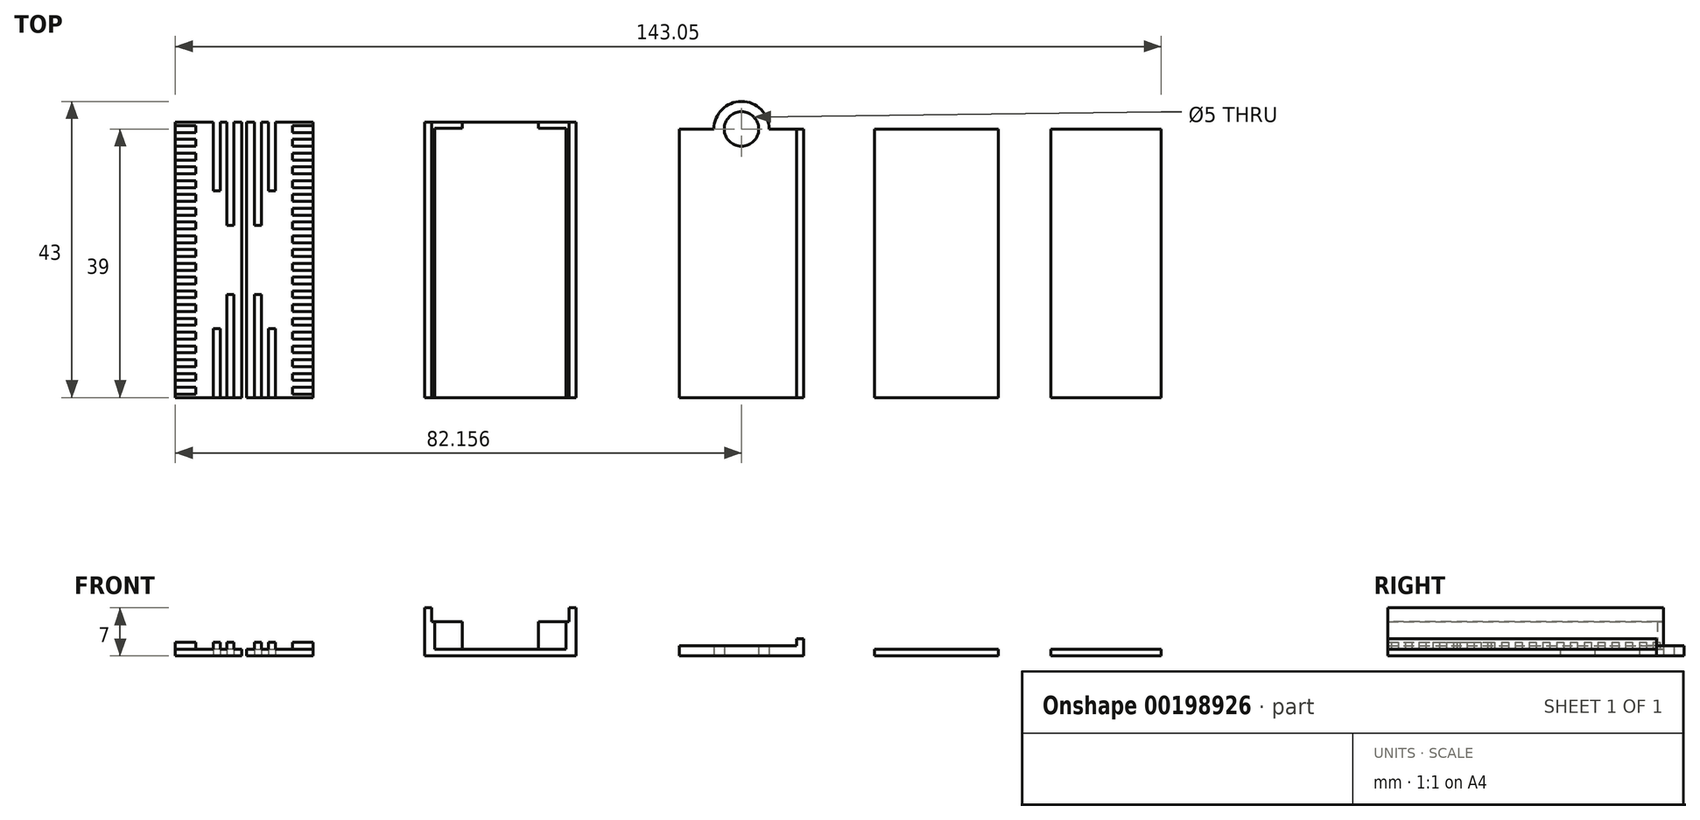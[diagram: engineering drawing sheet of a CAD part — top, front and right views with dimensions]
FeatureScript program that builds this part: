
annotation { "Feature Type Name" : "Feature", "Feature Type Description" : "" }
export const myFeature = defineFeature(function(context is Context, id is Id, definition is map)
    precondition{}
    {
        {
            var Q0;
            Q0=qCreatedBy(makeId("Top.planeOp"),FACE);
            var sketch = newSketch(context, id + "F0", { "sketchPlane" : qUnion([Q0])});
            skLineSegment(sketch, "E0.bottom", {"start": v(-54.83, 0) * mm, "end": v(-34.83, 0) * mm});
            skLineSegment(sketch, "E0.top", {"start": v(-54.83, 40) * mm, "end": v(-34.83, 40) * mm});
            skLineSegment(sketch, "E0.left", {"start": v(-54.83, 0) * mm, "end": v(-54.83, 40) * mm});
            skLineSegment(sketch, "E0.right", {"start": v(-34.83, 0) * mm, "end": v(-34.83, 40) * mm});
            skLineSegment(sketch, "E1.bottom", {"start": v(-18.67, 0) * mm, "end": v(3.33, 0) * mm});
            skLineSegment(sketch, "E1.top", {"start": v(-18.67, 40) * mm, "end": v(3.33, 40) * mm});
            skLineSegment(sketch, "E1.left", {"start": v(-18.67, 0) * mm, "end": v(-18.67, 40) * mm});
            skLineSegment(sketch, "E1.right", {"start": v(3.33, 0) * mm, "end": v(3.33, 40) * mm});
            skLineSegment(sketch, "E2.bottom", {"start": v(46.62, 0) * mm, "end": v(64.62, 0) * mm});
            skLineSegment(sketch, "E2.top", {"start": v(46.62, 39) * mm, "end": v(64.62, 39) * mm});
            skLineSegment(sketch, "E2.left", {"start": v(46.62, 0) * mm, "end": v(46.62, 39) * mm});
            skLineSegment(sketch, "E2.right", {"start": v(64.62, 0) * mm, "end": v(64.62, 39) * mm});
            skLineSegment(sketch, "E3.bottom", {"start": v(18.33, 0) * mm, "end": v(36.33, 0) * mm});
            skLineSegment(sketch, "E3.top", {"start": v(18.33, 39) * mm, "end": v(36.33, 39) * mm});
            skLineSegment(sketch, "E3.left", {"start": v(18.33, 0) * mm, "end": v(18.33, 39) * mm});
            skLineSegment(sketch, "E3.right", {"start": v(36.33, 0) * mm, "end": v(36.33, 39) * mm});
            skLineSegment(sketch, "E4.bottom", {"start": v(72.22, 0) * mm, "end": v(88.22, 0) * mm});
            skLineSegment(sketch, "E4.top", {"start": v(72.22, 39) * mm, "end": v(88.22, 39) * mm});
            skLineSegment(sketch, "E4.left", {"start": v(72.22, 0) * mm, "end": v(72.22, 39) * mm});
            skLineSegment(sketch, "E4.right", {"start": v(88.22, 0) * mm, "end": v(88.22, 39) * mm});
            skLineSegment(sketch, "E5", {"start": v(-17.67, 40) * mm, "end": v(-17.67, 0) * mm});
            skLineSegment(sketch, "E6", {"start": v(2.33, 40) * mm, "end": v(2.33, 0) * mm});
            skLineSegment(sketch, "E7", {"start": v(-17.17, 39.1) * mm, "end": v(-17.17, 0) * mm});
            skLineSegment(sketch, "E8", {"start": v(1.83, 39.1) * mm, "end": v(1.83, 0) * mm});
            skLineSegment(sketch, "E9", {"start": v(-44.83, 40) * mm, "end": v(-44.83, 0) * mm, "construction": true});
            skLineSegment(sketch, "E10.bottom", {"start": v(-44.48, 40) * mm, "end": v(-45.18, 40) * mm});
            skLineSegment(sketch, "E10.top", {"start": v(-44.48, 0) * mm, "end": v(-45.18, 0) * mm});
            skLineSegment(sketch, "E10.left", {"start": v(-44.48, 40) * mm, "end": v(-44.48, 0) * mm});
            skLineSegment(sketch, "E10.right", {"start": v(-45.18, 40) * mm, "end": v(-45.18, 0) * mm});
            skPoint(sketch, "E10.middle", {"position": v(-44.83, 20) * mm});
            skLineSegment(sketch, "E11", {"start": v(-46.83, 40) * mm, "end": v(-46.83, 0) * mm, "construction": true});
            skLineSegment(sketch, "E12", {"start": v(-48.83, 40) * mm, "end": v(-48.83, 0) * mm, "construction": true});
            skLineSegment(sketch, "E13.bottom", {"start": v(-46.33, 40) * mm, "end": v(-47.33, 40) * mm});
            skLineSegment(sketch, "E13.top", {"start": v(-46.33, 25) * mm, "end": v(-47.33, 25) * mm});
            skLineSegment(sketch, "E13.left", {"start": v(-46.33, 40) * mm, "end": v(-46.33, 25) * mm});
            skLineSegment(sketch, "E13.right", {"start": v(-47.33, 40) * mm, "end": v(-47.33, 25) * mm});
            skPoint(sketch, "E13.middle", {"position": v(-46.83, 32.5) * mm});
            skLineSegment(sketch, "E14.bottom", {"start": v(-48.33, 40) * mm, "end": v(-49.33, 40) * mm});
            skLineSegment(sketch, "E14.top", {"start": v(-48.33, 30) * mm, "end": v(-49.33, 30) * mm});
            skLineSegment(sketch, "E14.left", {"start": v(-48.33, 40) * mm, "end": v(-48.33, 30) * mm});
            skLineSegment(sketch, "E14.right", {"start": v(-49.33, 40) * mm, "end": v(-49.33, 30) * mm});
            skPoint(sketch, "E14.middle", {"position": v(-48.83, 35) * mm});
            skLineSegment(sketch, "E15", {"start": v(-34.83, 20) * mm, "end": v(-54.83, 20) * mm, "construction": true});
            skLineSegment(sketch, "E16.MirrorCS", {"start": v(-43.33, 40) * mm, "end": v(-42.33, 40) * mm});
            skLineSegment(sketch, "E17.MirrorCS", {"start": v(-41.33, 40) * mm, "end": v(-40.33, 40) * mm});
            skLineSegment(sketch, "E18.MirrorCS", {"start": v(-41.33, 30) * mm, "end": v(-40.33, 30) * mm});
            skLineSegment(sketch, "E19.MirrorCS", {"start": v(-43.33, 25) * mm, "end": v(-42.33, 25) * mm});
            skLineSegment(sketch, "E20.MirrorCS", {"start": v(-42.33, 40) * mm, "end": v(-42.33, 25) * mm});
            skLineSegment(sketch, "E21.MirrorCS", {"start": v(-40.33, 40) * mm, "end": v(-40.33, 30) * mm});
            skPoint(sketch, "E22.MirrorP", {"position": v(-40.83, 35) * mm});
            skLineSegment(sketch, "E23.MirrorCS", {"start": v(-43.33, 40) * mm, "end": v(-43.33, 25) * mm});
            skLineSegment(sketch, "E24.MirrorCS", {"start": v(-41.33, 40) * mm, "end": v(-41.33, 30) * mm});
            skPoint(sketch, "E25.MirrorP", {"position": v(-42.83, 32.5) * mm});
            skLineSegment(sketch, "E26.MirrorCS", {"start": v(-46.33, 0) * mm, "end": v(-47.33, 0) * mm});
            skLineSegment(sketch, "E27.MirrorCS", {"start": v(-41.33, 0) * mm, "end": v(-40.33, 0) * mm});
            skLineSegment(sketch, "E28.MirrorCS", {"start": v(-41.33, 10) * mm, "end": v(-40.33, 10) * mm});
            skLineSegment(sketch, "E29.MirrorCS", {"start": v(-48.33, 0) * mm, "end": v(-49.33, 0) * mm});
            skLineSegment(sketch, "E30.MirrorCS", {"start": v(-43.33, 0) * mm, "end": v(-42.33, 0) * mm});
            skLineSegment(sketch, "E31.MirrorCS", {"start": v(-48.33, 10) * mm, "end": v(-49.33, 10) * mm});
            skLineSegment(sketch, "E32.MirrorCS", {"start": v(-46.33, 15) * mm, "end": v(-47.33, 15) * mm});
            skLineSegment(sketch, "E33.MirrorCS", {"start": v(-43.33, 15) * mm, "end": v(-42.33, 15) * mm});
            skLineSegment(sketch, "E34.MirrorCS", {"start": v(-47.33, 0) * mm, "end": v(-47.33, 15) * mm});
            skLineSegment(sketch, "E35.MirrorCS", {"start": v(-49.33, 0) * mm, "end": v(-49.33, 10) * mm});
            skLineSegment(sketch, "E36.MirrorCS", {"start": v(-41.33, 0) * mm, "end": v(-41.33, 10) * mm});
            skPoint(sketch, "E37.MirrorP", {"position": v(-48.83, 5) * mm});
            skLineSegment(sketch, "E38.MirrorCS", {"start": v(-46.33, 0) * mm, "end": v(-46.33, 15) * mm});
            skLineSegment(sketch, "E39.MirrorCS", {"start": v(-48.33, 0) * mm, "end": v(-48.33, 10) * mm});
            skLineSegment(sketch, "E40.MirrorCS", {"start": v(-48.83, 0) * mm, "end": v(-48.83, 40) * mm, "construction": true});
            skLineSegment(sketch, "E41.MirrorCS", {"start": v(-43.33, 0) * mm, "end": v(-43.33, 15) * mm});
            skPoint(sketch, "E42.MirrorP", {"position": v(-40.83, 5) * mm});
            skPoint(sketch, "E43.MirrorP", {"position": v(-42.83, 7.5) * mm});
            skLineSegment(sketch, "E44.MirrorCS", {"start": v(-44.83, 0) * mm, "end": v(-44.83, 40) * mm, "construction": true});
            skLineSegment(sketch, "E45.MirrorCS", {"start": v(-45.18, 0) * mm, "end": v(-45.18, 40) * mm});
            skLineSegment(sketch, "E46.MirrorCS", {"start": v(-46.83, 0) * mm, "end": v(-46.83, 40) * mm, "construction": true});
            skLineSegment(sketch, "E47.MirrorCS", {"start": v(-42.33, 0) * mm, "end": v(-42.33, 15) * mm});
            skPoint(sketch, "E48.MirrorP", {"position": v(-46.83, 7.5) * mm});
            skLineSegment(sketch, "E49.MirrorCS", {"start": v(-44.48, 0) * mm, "end": v(-44.48, 40) * mm});
            skLineSegment(sketch, "E50.MirrorCS", {"start": v(-40.33, 0) * mm, "end": v(-40.33, 10) * mm});
            skLineSegment(sketch, "E51.bottom", {"start": v(-54.83, 39.5) * mm, "end": v(-51.83, 39.5) * mm});
            skLineSegment(sketch, "E51.top", {"start": v(-54.83, 38.5) * mm, "end": v(-51.83, 38.5) * mm});
            skLineSegment(sketch, "E51.left", {"start": v(-54.83, 39.5) * mm, "end": v(-54.83, 38.5) * mm});
            skLineSegment(sketch, "E51.right", {"start": v(-51.83, 39.5) * mm, "end": v(-51.83, 38.5) * mm});
            skLineSegment(sketch, "E52.0.1.0", {"start": v(-54.83, 37.5) * mm, "end": v(-51.83, 37.5) * mm});
            skLineSegment(sketch, "E52.0.1.1", {"start": v(-51.83, 37.5) * mm, "end": v(-51.83, 36.5) * mm});
            skLineSegment(sketch, "E52.0.1.2", {"start": v(-54.83, 36.5) * mm, "end": v(-51.83, 36.5) * mm});
            skLineSegment(sketch, "E52.0.2.0", {"start": v(-54.83, 35.5) * mm, "end": v(-51.83, 35.5) * mm});
            skLineSegment(sketch, "E52.0.2.1", {"start": v(-51.83, 35.5) * mm, "end": v(-51.83, 34.5) * mm});
            skLineSegment(sketch, "E52.0.2.2", {"start": v(-54.83, 34.5) * mm, "end": v(-51.83, 34.5) * mm});
            skLineSegment(sketch, "E52.0.3.0", {"start": v(-54.83, 33.5) * mm, "end": v(-51.83, 33.5) * mm});
            skLineSegment(sketch, "E52.0.3.1", {"start": v(-51.83, 33.5) * mm, "end": v(-51.83, 32.5) * mm});
            skLineSegment(sketch, "E52.0.3.2", {"start": v(-54.83, 32.5) * mm, "end": v(-51.83, 32.5) * mm});
            skLineSegment(sketch, "E52.0.4.0", {"start": v(-54.83, 31.5) * mm, "end": v(-51.83, 31.5) * mm});
            skLineSegment(sketch, "E52.0.4.1", {"start": v(-51.83, 31.5) * mm, "end": v(-51.83, 30.5) * mm});
            skLineSegment(sketch, "E52.0.4.2", {"start": v(-54.83, 30.5) * mm, "end": v(-51.83, 30.5) * mm});
            skLineSegment(sketch, "E52.0.5.0", {"start": v(-54.83, 29.5) * mm, "end": v(-51.83, 29.5) * mm});
            skLineSegment(sketch, "E52.0.5.1", {"start": v(-51.83, 29.5) * mm, "end": v(-51.83, 28.5) * mm});
            skLineSegment(sketch, "E52.0.5.2", {"start": v(-54.83, 28.5) * mm, "end": v(-51.83, 28.5) * mm});
            skLineSegment(sketch, "E52.0.6.0", {"start": v(-54.83, 27.5) * mm, "end": v(-51.83, 27.5) * mm});
            skLineSegment(sketch, "E52.0.6.1", {"start": v(-51.83, 27.5) * mm, "end": v(-51.83, 26.5) * mm});
            skLineSegment(sketch, "E52.0.6.2", {"start": v(-54.83, 26.5) * mm, "end": v(-51.83, 26.5) * mm});
            skLineSegment(sketch, "E52.0.7.0", {"start": v(-54.83, 25.5) * mm, "end": v(-51.83, 25.5) * mm});
            skLineSegment(sketch, "E52.0.7.1", {"start": v(-51.83, 25.5) * mm, "end": v(-51.83, 24.5) * mm});
            skLineSegment(sketch, "E52.0.7.2", {"start": v(-54.83, 24.5) * mm, "end": v(-51.83, 24.5) * mm});
            skLineSegment(sketch, "E52.0.8.0", {"start": v(-54.83, 23.5) * mm, "end": v(-51.83, 23.5) * mm});
            skLineSegment(sketch, "E52.0.8.1", {"start": v(-51.83, 23.5) * mm, "end": v(-51.83, 22.5) * mm});
            skLineSegment(sketch, "E52.0.8.2", {"start": v(-54.83, 22.5) * mm, "end": v(-51.83, 22.5) * mm});
            skLineSegment(sketch, "E52.0.9.0", {"start": v(-54.83, 21.5) * mm, "end": v(-51.83, 21.5) * mm});
            skLineSegment(sketch, "E52.0.9.1", {"start": v(-51.83, 21.5) * mm, "end": v(-51.83, 20.5) * mm});
            skLineSegment(sketch, "E52.0.9.2", {"start": v(-54.83, 20.5) * mm, "end": v(-51.83, 20.5) * mm});
            skLineSegment(sketch, "E52.0.10.0", {"start": v(-54.83, 19.5) * mm, "end": v(-51.83, 19.5) * mm});
            skLineSegment(sketch, "E52.0.10.1", {"start": v(-51.83, 19.5) * mm, "end": v(-51.83, 18.5) * mm});
            skLineSegment(sketch, "E52.0.10.2", {"start": v(-54.83, 18.5) * mm, "end": v(-51.83, 18.5) * mm});
            skLineSegment(sketch, "E52.0.11.0", {"start": v(-54.83, 17.5) * mm, "end": v(-51.83, 17.5) * mm});
            skLineSegment(sketch, "E52.0.11.1", {"start": v(-51.83, 17.5) * mm, "end": v(-51.83, 16.5) * mm});
            skLineSegment(sketch, "E52.0.11.2", {"start": v(-54.83, 16.5) * mm, "end": v(-51.83, 16.5) * mm});
            skLineSegment(sketch, "E52.0.12.0", {"start": v(-54.83, 15.5) * mm, "end": v(-51.83, 15.5) * mm});
            skLineSegment(sketch, "E52.0.12.1", {"start": v(-51.83, 15.5) * mm, "end": v(-51.83, 14.5) * mm});
            skLineSegment(sketch, "E52.0.12.2", {"start": v(-54.83, 14.5) * mm, "end": v(-51.83, 14.5) * mm});
            skLineSegment(sketch, "E52.0.13.0", {"start": v(-54.83, 13.5) * mm, "end": v(-51.83, 13.5) * mm});
            skLineSegment(sketch, "E52.0.13.1", {"start": v(-51.83, 13.5) * mm, "end": v(-51.83, 12.5) * mm});
            skLineSegment(sketch, "E52.0.13.2", {"start": v(-54.83, 12.5) * mm, "end": v(-51.83, 12.5) * mm});
            skLineSegment(sketch, "E52.0.14.0", {"start": v(-54.83, 11.5) * mm, "end": v(-51.83, 11.5) * mm});
            skLineSegment(sketch, "E52.0.14.1", {"start": v(-51.83, 11.5) * mm, "end": v(-51.83, 10.5) * mm});
            skLineSegment(sketch, "E52.0.14.2", {"start": v(-54.83, 10.5) * mm, "end": v(-51.83, 10.5) * mm});
            skLineSegment(sketch, "E52.0.15.0", {"start": v(-54.83, 9.5) * mm, "end": v(-51.83, 9.5) * mm});
            skLineSegment(sketch, "E52.0.15.1", {"start": v(-51.83, 9.5) * mm, "end": v(-51.83, 8.5) * mm});
            skLineSegment(sketch, "E52.0.15.2", {"start": v(-54.83, 8.5) * mm, "end": v(-51.83, 8.5) * mm});
            skLineSegment(sketch, "E52.0.16.0", {"start": v(-54.83, 7.5) * mm, "end": v(-51.83, 7.5) * mm});
            skLineSegment(sketch, "E52.0.16.1", {"start": v(-51.83, 7.5) * mm, "end": v(-51.83, 6.5) * mm});
            skLineSegment(sketch, "E52.0.16.2", {"start": v(-54.83, 6.5) * mm, "end": v(-51.83, 6.5) * mm});
            skLineSegment(sketch, "E52.0.17.0", {"start": v(-54.83, 5.5) * mm, "end": v(-51.83, 5.5) * mm});
            skLineSegment(sketch, "E52.0.17.1", {"start": v(-51.83, 5.5) * mm, "end": v(-51.83, 4.5) * mm});
            skLineSegment(sketch, "E52.0.17.2", {"start": v(-54.83, 4.5) * mm, "end": v(-51.83, 4.5) * mm});
            skLineSegment(sketch, "E52.0.18.0", {"start": v(-54.83, 3.5) * mm, "end": v(-51.83, 3.5) * mm});
            skLineSegment(sketch, "E52.0.18.1", {"start": v(-51.83, 3.5) * mm, "end": v(-51.83, 2.5) * mm});
            skLineSegment(sketch, "E52.0.18.2", {"start": v(-54.83, 2.5) * mm, "end": v(-51.83, 2.5) * mm});
            skLineSegment(sketch, "E52.0.19.0", {"start": v(-54.83, 1.5) * mm, "end": v(-51.83, 1.5) * mm});
            skLineSegment(sketch, "E52.0.19.1", {"start": v(-51.83, 1.5) * mm, "end": v(-51.83, 0.5) * mm});
            skLineSegment(sketch, "E52.0.19.2", {"start": v(-54.83, 0.5) * mm, "end": v(-51.83, 0.5) * mm});
            skLineSegment(sketch, "E52.direction1", {"start": v(-54.83, 39.5) * mm, "end": v(-51.93, 39.5) * mm, "construction": true});
            skLineSegment(sketch, "E52.direction2", {"start": v(-54.83, 39.5) * mm, "end": v(-54.83, 37.5) * mm, "construction": true});
            skLineSegment(sketch, "E53.MirrorCS", {"start": v(-37.83, 27.5) * mm, "end": v(-37.83, 26.5) * mm});
            skLineSegment(sketch, "E54.MirrorCS", {"start": v(-37.83, 19.5) * mm, "end": v(-37.83, 18.5) * mm});
            skLineSegment(sketch, "E55.MirrorCS", {"start": v(-37.83, 15.5) * mm, "end": v(-37.83, 14.5) * mm});
            skLineSegment(sketch, "E56.MirrorCS", {"start": v(-37.83, 9.5) * mm, "end": v(-37.83, 8.5) * mm});
            skLineSegment(sketch, "E57.MirrorCS", {"start": v(-37.83, 31.5) * mm, "end": v(-37.83, 30.5) * mm});
            skLineSegment(sketch, "E58.MirrorCS", {"start": v(-37.83, 21.5) * mm, "end": v(-37.83, 20.5) * mm});
            skLineSegment(sketch, "E59.MirrorCS", {"start": v(-37.83, 37.5) * mm, "end": v(-37.83, 36.5) * mm});
            skLineSegment(sketch, "E60.MirrorCS", {"start": v(-37.83, 25.5) * mm, "end": v(-37.83, 24.5) * mm});
            skLineSegment(sketch, "E61.MirrorCS", {"start": v(-37.83, 11.5) * mm, "end": v(-37.83, 10.5) * mm});
            skLineSegment(sketch, "E62.MirrorCS", {"start": v(-37.83, 35.5) * mm, "end": v(-37.83, 34.5) * mm});
            skLineSegment(sketch, "E63.MirrorCS", {"start": v(-37.83, 23.5) * mm, "end": v(-37.83, 22.5) * mm});
            skLineSegment(sketch, "E64.MirrorCS", {"start": v(-37.83, 13.5) * mm, "end": v(-37.83, 12.5) * mm});
            skLineSegment(sketch, "E65.MirrorCS", {"start": v(-37.83, 29.5) * mm, "end": v(-37.83, 28.5) * mm});
            skLineSegment(sketch, "E66.MirrorCS", {"start": v(-37.83, 17.5) * mm, "end": v(-37.83, 16.5) * mm});
            skLineSegment(sketch, "E67.MirrorCS", {"start": v(-37.83, 33.5) * mm, "end": v(-37.83, 32.5) * mm});
            skLineSegment(sketch, "E68.MirrorCS", {"start": v(-37.83, 39.5) * mm, "end": v(-37.83, 38.5) * mm});
            skLineSegment(sketch, "E69.MirrorCS", {"start": v(-34.83, 39.5) * mm, "end": v(-37.83, 39.5) * mm});
            skLineSegment(sketch, "E70.MirrorCS", {"start": v(-34.83, 16.5) * mm, "end": v(-37.83, 16.5) * mm});
            skLineSegment(sketch, "E71.MirrorCS", {"start": v(-34.83, 37.5) * mm, "end": v(-37.83, 37.5) * mm});
            skLineSegment(sketch, "E72.MirrorCS", {"start": v(-34.83, 36.5) * mm, "end": v(-37.83, 36.5) * mm});
            skLineSegment(sketch, "E73.MirrorCS", {"start": v(-34.83, 29.5) * mm, "end": v(-37.83, 29.5) * mm});
            skLineSegment(sketch, "E74.MirrorCS", {"start": v(-34.83, 8.5) * mm, "end": v(-37.83, 8.5) * mm});
            skLineSegment(sketch, "E75.MirrorCS", {"start": v(-54.83, 20) * mm, "end": v(-34.83, 20) * mm, "construction": true});
            skLineSegment(sketch, "E76.MirrorCS", {"start": v(-34.83, 25.5) * mm, "end": v(-37.83, 25.5) * mm});
            skLineSegment(sketch, "E77.MirrorCS", {"start": v(-34.83, 19.5) * mm, "end": v(-37.83, 19.5) * mm});
            skLineSegment(sketch, "E78.MirrorCS", {"start": v(-34.83, 30.5) * mm, "end": v(-37.83, 30.5) * mm});
            skLineSegment(sketch, "E79.MirrorCS", {"start": v(-34.83, 20.5) * mm, "end": v(-37.83, 20.5) * mm});
            skLineSegment(sketch, "E80.MirrorCS", {"start": v(-34.83, 9.5) * mm, "end": v(-37.83, 9.5) * mm});
            skLineSegment(sketch, "E81.MirrorCS", {"start": v(-34.83, 10.5) * mm, "end": v(-37.83, 10.5) * mm});
            skLineSegment(sketch, "E82.MirrorCS", {"start": v(-34.83, 39.5) * mm, "end": v(-37.73, 39.5) * mm, "construction": true});
            skLineSegment(sketch, "E83.MirrorCS", {"start": v(-34.83, 15.5) * mm, "end": v(-37.83, 15.5) * mm});
            skLineSegment(sketch, "E84.MirrorCS", {"start": v(-34.83, 26.5) * mm, "end": v(-37.83, 26.5) * mm});
            skLineSegment(sketch, "E85.MirrorCS", {"start": v(-34.83, 31.5) * mm, "end": v(-37.83, 31.5) * mm});
            skLineSegment(sketch, "E86.MirrorCS", {"start": v(-34.83, 35.5) * mm, "end": v(-37.83, 35.5) * mm});
            skLineSegment(sketch, "E87.MirrorCS", {"start": v(-34.83, 14.5) * mm, "end": v(-37.83, 14.5) * mm});
            skLineSegment(sketch, "E88.MirrorCS", {"start": v(-34.83, 21.5) * mm, "end": v(-37.83, 21.5) * mm});
            skLineSegment(sketch, "E89.MirrorCS", {"start": v(-34.83, 32.5) * mm, "end": v(-37.83, 32.5) * mm});
            skLineSegment(sketch, "E90.MirrorCS", {"start": v(-34.83, 13.5) * mm, "end": v(-37.83, 13.5) * mm});
            skLineSegment(sketch, "E91.MirrorCS", {"start": v(-34.83, 24.5) * mm, "end": v(-37.83, 24.5) * mm});
            skLineSegment(sketch, "E92.MirrorCS", {"start": v(-34.83, 33.5) * mm, "end": v(-37.83, 33.5) * mm});
            skLineSegment(sketch, "E93.MirrorCS", {"start": v(-34.83, 12.5) * mm, "end": v(-37.83, 12.5) * mm});
            skLineSegment(sketch, "E94.MirrorCS", {"start": v(-34.83, 23.5) * mm, "end": v(-37.83, 23.5) * mm});
            skLineSegment(sketch, "E95.MirrorCS", {"start": v(-34.83, 18.5) * mm, "end": v(-37.83, 18.5) * mm});
            skLineSegment(sketch, "E96.MirrorCS", {"start": v(-34.83, 38.5) * mm, "end": v(-37.83, 38.5) * mm});
            skLineSegment(sketch, "E97.MirrorCS", {"start": v(-34.83, 27.5) * mm, "end": v(-37.83, 27.5) * mm});
            skLineSegment(sketch, "E98.MirrorCS", {"start": v(-34.83, 34.5) * mm, "end": v(-37.83, 34.5) * mm});
            skLineSegment(sketch, "E99.MirrorCS", {"start": v(-34.83, 11.5) * mm, "end": v(-37.83, 11.5) * mm});
            skLineSegment(sketch, "E100.MirrorCS", {"start": v(-34.83, 17.5) * mm, "end": v(-37.83, 17.5) * mm});
            skLineSegment(sketch, "E101.MirrorCS", {"start": v(-34.83, 28.5) * mm, "end": v(-37.83, 28.5) * mm});
            skLineSegment(sketch, "E102.MirrorCS", {"start": v(-34.83, 22.5) * mm, "end": v(-37.83, 22.5) * mm});
            skLineSegment(sketch, "E103.MirrorCS", {"start": v(-37.83, 1.5) * mm, "end": v(-37.83, 0.5) * mm});
            skLineSegment(sketch, "E104.MirrorCS", {"start": v(-34.83, 1.5) * mm, "end": v(-37.83, 1.5) * mm});
            skLineSegment(sketch, "E105.MirrorCS", {"start": v(-37.83, 7.5) * mm, "end": v(-37.83, 6.5) * mm});
            skLineSegment(sketch, "E106.MirrorCS", {"start": v(-34.83, 5.5) * mm, "end": v(-37.83, 5.5) * mm});
            skLineSegment(sketch, "E107.MirrorCS", {"start": v(-34.83, 4.5) * mm, "end": v(-37.83, 4.5) * mm});
            skLineSegment(sketch, "E108.MirrorCS", {"start": v(-34.83, 7.5) * mm, "end": v(-37.83, 7.5) * mm});
            skLineSegment(sketch, "E109.MirrorCS", {"start": v(-37.83, 5.5) * mm, "end": v(-37.83, 4.5) * mm});
            skLineSegment(sketch, "E110.MirrorCS", {"start": v(-34.83, 3.5) * mm, "end": v(-37.83, 3.5) * mm});
            skLineSegment(sketch, "E111.MirrorCS", {"start": v(-37.83, 3.5) * mm, "end": v(-37.83, 2.5) * mm});
            skLineSegment(sketch, "E112.MirrorCS", {"start": v(-34.83, 2.5) * mm, "end": v(-37.83, 2.5) * mm});
            skLineSegment(sketch, "E113.MirrorCS", {"start": v(-34.83, 0.5) * mm, "end": v(-37.83, 0.5) * mm});
            skLineSegment(sketch, "E114.MirrorCS", {"start": v(-34.83, 6.5) * mm, "end": v(-37.83, 6.5) * mm});
            skCircle(sketch, "E115", {"center": v(27.33, 39) * mm, "radius": 2.5 * mm});
            skCircle(sketch, "E116", {"center": v(27.33, 39) * mm, "radius": 4 * mm});
            skLineSegment(sketch, "E117", {"start": v(35.33, 39) * mm, "end": v(35.33, 0) * mm});
            skLineSegment(sketch, "E118.bottom", {"start": v(1.83, 40) * mm, "end": v(-2.17, 40) * mm});
            skLineSegment(sketch, "E118.top", {"start": v(1.83, 39.1) * mm, "end": v(-2.17, 39.1) * mm});
            skLineSegment(sketch, "E118.right", {"start": v(-2.17, 40) * mm, "end": v(-2.17, 39.1) * mm});
            skLineSegment(sketch, "E119.bottom", {"start": v(-17.17, 40) * mm, "end": v(-13.17, 40) * mm});
            skLineSegment(sketch, "E119.top", {"start": v(-17.17, 39.1) * mm, "end": v(-13.17, 39.1) * mm});
            skLineSegment(sketch, "E119.right", {"start": v(-13.17, 40) * mm, "end": v(-13.17, 39.1) * mm});
            skSolve(sketch);
        }
        {
            var Q0;
            {var subQ0=sQuery(id+"F0.wireOp",EDGE,"E52.0.10.0");Q0=makeQuery(id+"F0.imprint","IMPRINT",FACE,{"disambiguationData":[TD([[makeQuery(id+"F0.imprint","IMPRINT",EDGE,{"derivedFrom":subQ0}),-1.0]])]});}
            var Q1;
            {var subQ0=sQuery(id+"F0.wireOp",EDGE,"E52.0.11.0");Q1=makeQuery(id+"F0.imprint","IMPRINT",FACE,{"disambiguationData":[TD([[makeQuery(id+"F0.imprint","IMPRINT",EDGE,{"derivedFrom":subQ0}),-1.0]])]});}
            var Q2;
            Q2=makeQuery(id+"F0.imprint","IMPRINT",FACE,{"disambiguationData":[TD([[makeQuery(id+"F0.imprint","IMPRINT",EDGE,{"derivedFrom":sQuery(id+"F0.wireOp",EDGE,"E61.MirrorCS")}),1.0]])]});
            var Q3;
            {var subQ0=sQuery(id+"F0.wireOp",EDGE,"E52.0.12.0");Q3=makeQuery(id+"F0.imprint","IMPRINT",FACE,{"disambiguationData":[TD([[makeQuery(id+"F0.imprint","IMPRINT",EDGE,{"derivedFrom":subQ0}),-1.0]])]});}
            var Q4;
            {var subQ0=sQuery(id+"F0.wireOp",EDGE,"E52.0.13.0");Q4=makeQuery(id+"F0.imprint","IMPRINT",FACE,{"disambiguationData":[TD([[makeQuery(id+"F0.imprint","IMPRINT",EDGE,{"derivedFrom":subQ0}),-1.0]])]});}
            var Q5;
            Q5=makeQuery(id+"F0.imprint","IMPRINT",FACE,{"disambiguationData":[TD([[makeQuery(id+"F0.imprint","IMPRINT",EDGE,{"derivedFrom":sQuery(id+"F0.wireOp",EDGE,"E65.MirrorCS")}),1.0]])]});
            var Q6;
            {var subQ0=sQuery(id+"F0.wireOp",EDGE,"E106.MirrorCS");Q6=makeQuery(id+"F0.imprint","IMPRINT",FACE,{"disambiguationData":[TD([[makeQuery(id+"F0.imprint","IMPRINT",EDGE,{"derivedFrom":subQ0}),1.0]])]});}
            var Q7;
            Q7=makeQuery(id+"F0.imprint","IMPRINT",FACE,{"disambiguationData":[TD([[makeQuery(id+"F0.imprint","IMPRINT",EDGE,{"derivedFrom":sQuery(id+"F0.wireOp",EDGE,"E66.MirrorCS")}),1.0]])]});
            var Q8;
            Q8=makeQuery(id+"F0.imprint","IMPRINT",FACE,{"disambiguationData":[TD([[makeQuery(id+"F0.imprint","IMPRINT",EDGE,{"derivedFrom":sQuery(id+"F0.wireOp",EDGE,"E16.MirrorCS")}),-1.0]])]});
            var Q9;
            Q9=makeQuery(id+"F0.imprint","IMPRINT",FACE,{"disambiguationData":[TD([[makeQuery(id+"F0.imprint","IMPRINT",EDGE,{"derivedFrom":sQuery(id+"F0.wireOp",EDGE,"E51.bottom")}),-1.0]])]});
            var Q10;
            {var subQ0=sQuery(id+"F0.wireOp",EDGE,"E110.MirrorCS");Q10=makeQuery(id+"F0.imprint","IMPRINT",FACE,{"disambiguationData":[TD([[makeQuery(id+"F0.imprint","IMPRINT",EDGE,{"derivedFrom":subQ0}),1.0]])]});}
            var Q11;
            Q11=makeQuery(id+"F0.imprint","IMPRINT",FACE,{"disambiguationData":[TD([[makeQuery(id+"F0.imprint","IMPRINT",EDGE,{"derivedFrom":sQuery(id+"F0.wireOp",EDGE,"E62.MirrorCS")}),1.0]])]});
            var Q12;
            {var subQ0=sQuery(id+"F0.wireOp",EDGE,"E52.0.14.0");Q12=makeQuery(id+"F0.imprint","IMPRINT",FACE,{"disambiguationData":[TD([[makeQuery(id+"F0.imprint","IMPRINT",EDGE,{"derivedFrom":subQ0}),-1.0]])]});}
            var Q13;
            Q13=makeQuery(id+"F0.imprint","IMPRINT",FACE,{"disambiguationData":[TD([[makeQuery(id+"F0.imprint","IMPRINT",EDGE,{"derivedFrom":sQuery(id+"F0.wireOp",EDGE,"E59.MirrorCS")}),1.0]])]});
            var Q14;
            Q14=makeQuery(id+"F0.imprint","IMPRINT",FACE,{"disambiguationData":[TD([[makeQuery(id+"F0.imprint","IMPRINT",EDGE,{"derivedFrom":sQuery(id+"F0.wireOp",EDGE,"E10.bottom")}),1.0]])]});
            var Q15;
            {var subQ0=sQuery(id+"F0.wireOp",EDGE,"E52.0.15.0");Q15=makeQuery(id+"F0.imprint","IMPRINT",FACE,{"disambiguationData":[TD([[makeQuery(id+"F0.imprint","IMPRINT",EDGE,{"derivedFrom":subQ0}),-1.0]])]});}
            var Q16;
            {var subQ0=sQuery(id+"F0.wireOp",EDGE,"E52.0.16.0");Q16=makeQuery(id+"F0.imprint","IMPRINT",FACE,{"disambiguationData":[TD([[makeQuery(id+"F0.imprint","IMPRINT",EDGE,{"derivedFrom":subQ0}),-1.0]])]});}
            var Q17;
            Q17=makeQuery(id+"F0.imprint","IMPRINT",FACE,{"disambiguationData":[TD([[makeQuery(id+"F0.imprint","IMPRINT",EDGE,{"derivedFrom":sQuery(id+"F0.wireOp",EDGE,"E13.bottom")}),1.0]])]});
            var Q18;
            Q18=makeQuery(id+"F0.imprint","IMPRINT",FACE,{"disambiguationData":[TD([[makeQuery(id+"F0.imprint","IMPRINT",EDGE,{"derivedFrom":sQuery(id+"F0.wireOp",EDGE,"E64.MirrorCS")}),1.0]])]});
            var Q19;
            {var subQ0=sQuery(id+"F0.wireOp",EDGE,"E52.0.17.0");Q19=makeQuery(id+"F0.imprint","IMPRINT",FACE,{"disambiguationData":[TD([[makeQuery(id+"F0.imprint","IMPRINT",EDGE,{"derivedFrom":subQ0}),-1.0]])]});}
            var Q20;
            {var subQ0=sQuery(id+"F0.wireOp",EDGE,"E52.0.18.0");Q20=makeQuery(id+"F0.imprint","IMPRINT",FACE,{"disambiguationData":[TD([[makeQuery(id+"F0.imprint","IMPRINT",EDGE,{"derivedFrom":subQ0}),-1.0]])]});}
            var Q21;
            {var subQ0=sQuery(id+"F0.wireOp",EDGE,"E52.0.6.0");Q21=makeQuery(id+"F0.imprint","IMPRINT",FACE,{"disambiguationData":[TD([[makeQuery(id+"F0.imprint","IMPRINT",EDGE,{"derivedFrom":subQ0}),-1.0]])]});}
            var Q22;
            Q22=makeQuery(id+"F0.imprint","IMPRINT",FACE,{"disambiguationData":[TD([[makeQuery(id+"F0.imprint","IMPRINT",EDGE,{"derivedFrom":sQuery(id+"F0.wireOp",EDGE,"E28.MirrorCS")}),-1.0]])]});
            var Q23;
            Q23=makeQuery(id+"F0.imprint","IMPRINT",FACE,{"disambiguationData":[TD([[makeQuery(id+"F0.imprint","IMPRINT",EDGE,{"derivedFrom":sQuery(id+"F0.wireOp",EDGE,"E58.MirrorCS")}),1.0]])]});
            var Q24;
            {var subQ0=sQuery(id+"F0.wireOp",EDGE,"E52.0.19.0");Q24=makeQuery(id+"F0.imprint","IMPRINT",FACE,{"disambiguationData":[TD([[makeQuery(id+"F0.imprint","IMPRINT",EDGE,{"derivedFrom":subQ0}),-1.0]])]});}
            var Q25;
            {var subQ0=sQuery(id+"F0.wireOp",EDGE,"E52.0.8.0");Q25=makeQuery(id+"F0.imprint","IMPRINT",FACE,{"disambiguationData":[TD([[makeQuery(id+"F0.imprint","IMPRINT",EDGE,{"derivedFrom":subQ0}),-1.0]])]});}
            var Q26;
            {var subQ0=sQuery(id+"F0.wireOp",EDGE,"E52.0.9.0");Q26=makeQuery(id+"F0.imprint","IMPRINT",FACE,{"disambiguationData":[TD([[makeQuery(id+"F0.imprint","IMPRINT",EDGE,{"derivedFrom":subQ0}),-1.0]])]});}
            var Q27;
            {var subQ0=sQuery(id+"F0.wireOp",EDGE,"E52.0.7.0");Q27=makeQuery(id+"F0.imprint","IMPRINT",FACE,{"disambiguationData":[TD([[makeQuery(id+"F0.imprint","IMPRINT",EDGE,{"derivedFrom":subQ0}),-1.0]])]});}
            var Q28;
            Q28=makeQuery(id+"F0.imprint","IMPRINT",FACE,{"disambiguationData":[TD([[makeQuery(id+"F0.imprint","IMPRINT",EDGE,{"derivedFrom":sQuery(id+"F0.wireOp",EDGE,"E103.MirrorCS")}),1.0]])]});
            var Q29;
            Q29=makeQuery(id+"F0.imprint","IMPRINT",FACE,{"disambiguationData":[TD([[makeQuery(id+"F0.imprint","IMPRINT",EDGE,{"derivedFrom":sQuery(id+"F0.wireOp",EDGE,"E67.MirrorCS")}),1.0]])]});
            var Q30;
            {var subQ0=sQuery(id+"F0.wireOp",EDGE,"E52.0.5.0");Q30=makeQuery(id+"F0.imprint","IMPRINT",FACE,{"disambiguationData":[TD([[makeQuery(id+"F0.imprint","IMPRINT",EDGE,{"derivedFrom":subQ0}),-1.0]])]});}
            var Q31;
            Q31=makeQuery(id+"F0.imprint","IMPRINT",FACE,{"disambiguationData":[TD([[makeQuery(id+"F0.imprint","IMPRINT",EDGE,{"derivedFrom":sQuery(id+"F0.wireOp",EDGE,"E31.MirrorCS")}),1.0]])]});
            var Q32;
            Q32=makeQuery(id+"F0.imprint","IMPRINT",FACE,{"disambiguationData":[TD([[makeQuery(id+"F0.imprint","IMPRINT",EDGE,{"derivedFrom":sQuery(id+"F0.wireOp",EDGE,"E63.MirrorCS")}),1.0]])]});
            var Q33;
            {var subQ0=sQuery(id+"F0.wireOp",EDGE,"E52.0.4.0");Q33=makeQuery(id+"F0.imprint","IMPRINT",FACE,{"disambiguationData":[TD([[makeQuery(id+"F0.imprint","IMPRINT",EDGE,{"derivedFrom":subQ0}),-1.0]])]});}
            var Q34;
            Q34=makeQuery(id+"F0.imprint","IMPRINT",FACE,{"disambiguationData":[TD([[makeQuery(id+"F0.imprint","IMPRINT",EDGE,{"derivedFrom":sQuery(id+"F0.wireOp",EDGE,"E60.MirrorCS")}),1.0]])]});
            var Q35;
            Q35=makeQuery(id+"F0.imprint","IMPRINT",FACE,{"disambiguationData":[TD([[makeQuery(id+"F0.imprint","IMPRINT",EDGE,{"derivedFrom":sQuery(id+"F0.wireOp",EDGE,"E32.MirrorCS")}),1.0]])]});
            var Q36;
            {var subQ0=sQuery(id+"F0.wireOp",EDGE,"E52.0.3.0");Q36=makeQuery(id+"F0.imprint","IMPRINT",FACE,{"disambiguationData":[TD([[makeQuery(id+"F0.imprint","IMPRINT",EDGE,{"derivedFrom":subQ0}),-1.0]])]});}
            var Q37;
            Q37=makeQuery(id+"F0.imprint","IMPRINT",FACE,{"disambiguationData":[TD([[makeQuery(id+"F0.imprint","IMPRINT",EDGE,{"derivedFrom":sQuery(id+"F0.wireOp",EDGE,"E33.MirrorCS")}),-1.0]])]});
            var Q38;
            Q38=makeQuery(id+"F0.imprint","IMPRINT",FACE,{"disambiguationData":[TD([[makeQuery(id+"F0.imprint","IMPRINT",EDGE,{"derivedFrom":sQuery(id+"F0.wireOp",EDGE,"E53.MirrorCS")}),1.0]])]});
            var Q39;
            Q39=makeQuery(id+"F0.imprint","IMPRINT",FACE,{"disambiguationData":[TD([[makeQuery(id+"F0.imprint","IMPRINT",EDGE,{"derivedFrom":sQuery(id+"F0.wireOp",EDGE,"E57.MirrorCS")}),1.0]])]});
            var Q40;
            {var subQ0=sQuery(id+"F0.wireOp",EDGE,"E52.0.1.0");Q40=makeQuery(id+"F0.imprint","IMPRINT",FACE,{"disambiguationData":[TD([[makeQuery(id+"F0.imprint","IMPRINT",EDGE,{"derivedFrom":subQ0}),-1.0]])]});}
            var Q41;
            {var subQ0=sQuery(id+"F0.wireOp",EDGE,"E52.0.2.0");Q41=makeQuery(id+"F0.imprint","IMPRINT",FACE,{"disambiguationData":[TD([[makeQuery(id+"F0.imprint","IMPRINT",EDGE,{"derivedFrom":subQ0}),-1.0]])]});}
            var Q42;
            Q42=makeQuery(id+"F0.imprint","IMPRINT",FACE,{"disambiguationData":[TD([[makeQuery(id+"F0.imprint","IMPRINT",EDGE,{"derivedFrom":sQuery(id+"F0.wireOp",EDGE,"E55.MirrorCS")}),1.0]])]});
            var Q43;
            Q43=makeQuery(id+"F0.imprint","IMPRINT",FACE,{"disambiguationData":[TD([[makeQuery(id+"F0.imprint","IMPRINT",EDGE,{"derivedFrom":sQuery(id+"F0.wireOp",EDGE,"E14.bottom")}),1.0]])]});
            var Q44;
            Q44=makeQuery(id+"F0.imprint","IMPRINT",FACE,{"disambiguationData":[TD([[makeQuery(id+"F0.imprint","IMPRINT",EDGE,{"derivedFrom":sQuery(id+"F0.wireOp",EDGE,"E56.MirrorCS")}),1.0]])]});
            var Q45;
            Q45=makeQuery(id+"F0.imprint","IMPRINT",FACE,{"disambiguationData":[TD([[makeQuery(id+"F0.imprint","IMPRINT",EDGE,{"derivedFrom":sQuery(id+"F0.wireOp",EDGE,"E18.MirrorCS")}),-1.0]])]});
            var Q46;
            Q46=makeQuery(id+"F0.imprint","IMPRINT",FACE,{"disambiguationData":[TD([[makeQuery(id+"F0.imprint","IMPRINT",EDGE,{"derivedFrom":sQuery(id+"F0.wireOp",EDGE,"E54.MirrorCS")}),1.0]])]});
            var Q47;
            Q47=makeQuery(id+"F0.imprint","IMPRINT",FACE,{"disambiguationData":[TD([[makeQuery(id+"F0.imprint","IMPRINT",EDGE,{"derivedFrom":sQuery(id+"F0.wireOp",EDGE,"E13.top")}),1.0]])]});
            var Q48;
            Q48=makeQuery(id+"F0.imprint","IMPRINT",FACE,{"disambiguationData":[TD([[makeQuery(id+"F0.imprint","IMPRINT",EDGE,{"derivedFrom":sQuery(id+"F0.wireOp",EDGE,"E68.MirrorCS")}),1.0]])]});
            var Q49;
            Q49=makeQuery(id+"F0.imprint","IMPRINT",FACE,{"disambiguationData":[TD([[makeQuery(id+"F0.imprint","IMPRINT",EDGE,{"derivedFrom":sQuery(id+"F0.wireOp",EDGE,"E105.MirrorCS")}),1.0]])]});
            var Q50;
            Q50=makeQuery(id+"F0.imprint","IMPRINT",FACE,{"disambiguationData":[TD([[makeQuery(id+"F0.imprint","IMPRINT",EDGE,{"derivedFrom":sQuery(id+"F0.wireOp",EDGE,"E17.MirrorCS")}),-1.0]])]});
            extrude(context, id + "F1", {"entities" : qUnion([Q0, Q1, Q2, Q3, Q4, Q5, Q6, Q7, Q8, Q9, Q10, Q11, Q12, Q13, Q14, Q15, Q16, Q17, Q18, Q19, Q20, Q21, Q22, Q23, Q24, Q25, Q26, Q27, Q28, Q29, Q30, Q31, Q32, Q33, Q34, Q35, Q36, Q37, Q38, Q39, Q40, Q41, Q42, Q43, Q44, Q45, Q46, Q47, Q48, Q49, Q50]), "depth" : 1 * mm});
        }
        {
            var Q0;
            Q0=makeQuery(id+"F0.imprint","IMPRINT",FACE,{"disambiguationData":[TD([[makeQuery(id+"F0.imprint","IMPRINT",EDGE,{"derivedFrom":sQuery(id+"F0.wireOp",EDGE,"E61.MirrorCS")}),1.0]])]});
            var Q1;
            Q1=makeQuery(id+"F0.imprint","IMPRINT",FACE,{"disambiguationData":[TD([[makeQuery(id+"F0.imprint","IMPRINT",EDGE,{"derivedFrom":sQuery(id+"F0.wireOp",EDGE,"E56.MirrorCS")}),1.0]])]});
            var Q2;
            Q2=makeQuery(id+"F0.imprint","IMPRINT",FACE,{"disambiguationData":[TD([[makeQuery(id+"F0.imprint","IMPRINT",EDGE,{"derivedFrom":sQuery(id+"F0.wireOp",EDGE,"E105.MirrorCS")}),1.0]])]});
            var Q3;
            {var subQ0=sQuery(id+"F0.wireOp",EDGE,"E106.MirrorCS");Q3=makeQuery(id+"F0.imprint","IMPRINT",FACE,{"disambiguationData":[TD([[makeQuery(id+"F0.imprint","IMPRINT",EDGE,{"derivedFrom":subQ0}),1.0]])]});}
            var Q4;
            {var subQ0=sQuery(id+"F0.wireOp",EDGE,"E110.MirrorCS");Q4=makeQuery(id+"F0.imprint","IMPRINT",FACE,{"disambiguationData":[TD([[makeQuery(id+"F0.imprint","IMPRINT",EDGE,{"derivedFrom":subQ0}),1.0]])]});}
            var Q5;
            Q5=makeQuery(id+"F0.imprint","IMPRINT",FACE,{"disambiguationData":[TD([[makeQuery(id+"F0.imprint","IMPRINT",EDGE,{"derivedFrom":sQuery(id+"F0.wireOp",EDGE,"E103.MirrorCS")}),1.0]])]});
            var Q6;
            Q6=makeQuery(id+"F0.imprint","IMPRINT",FACE,{"disambiguationData":[TD([[makeQuery(id+"F0.imprint","IMPRINT",EDGE,{"derivedFrom":sQuery(id+"F0.wireOp",EDGE,"E28.MirrorCS")}),-1.0]])]});
            var Q7;
            Q7=makeQuery(id+"F0.imprint","IMPRINT",FACE,{"disambiguationData":[TD([[makeQuery(id+"F0.imprint","IMPRINT",EDGE,{"derivedFrom":sQuery(id+"F0.wireOp",EDGE,"E33.MirrorCS")}),-1.0]])]});
            var Q8;
            Q8=makeQuery(id+"F0.imprint","IMPRINT",FACE,{"disambiguationData":[TD([[makeQuery(id+"F0.imprint","IMPRINT",EDGE,{"derivedFrom":sQuery(id+"F0.wireOp",EDGE,"E10.bottom")}),1.0]])]});
            var Q9;
            Q9=makeQuery(id+"F0.imprint","IMPRINT",FACE,{"disambiguationData":[TD([[makeQuery(id+"F0.imprint","IMPRINT",EDGE,{"derivedFrom":sQuery(id+"F0.wireOp",EDGE,"E32.MirrorCS")}),1.0]])]});
            var Q10;
            Q10=makeQuery(id+"F0.imprint","IMPRINT",FACE,{"disambiguationData":[TD([[makeQuery(id+"F0.imprint","IMPRINT",EDGE,{"derivedFrom":sQuery(id+"F0.wireOp",EDGE,"E31.MirrorCS")}),1.0]])]});
            var Q11;
            {var subQ0=sQuery(id+"F0.wireOp",EDGE,"E52.0.19.0");Q11=makeQuery(id+"F0.imprint","IMPRINT",FACE,{"disambiguationData":[TD([[makeQuery(id+"F0.imprint","IMPRINT",EDGE,{"derivedFrom":subQ0}),-1.0]])]});}
            var Q12;
            {var subQ0=sQuery(id+"F0.wireOp",EDGE,"E52.0.18.0");Q12=makeQuery(id+"F0.imprint","IMPRINT",FACE,{"disambiguationData":[TD([[makeQuery(id+"F0.imprint","IMPRINT",EDGE,{"derivedFrom":subQ0}),-1.0]])]});}
            var Q13;
            {var subQ0=sQuery(id+"F0.wireOp",EDGE,"E52.0.17.0");Q13=makeQuery(id+"F0.imprint","IMPRINT",FACE,{"disambiguationData":[TD([[makeQuery(id+"F0.imprint","IMPRINT",EDGE,{"derivedFrom":subQ0}),-1.0]])]});}
            var Q14;
            {var subQ0=sQuery(id+"F0.wireOp",EDGE,"E52.0.16.0");Q14=makeQuery(id+"F0.imprint","IMPRINT",FACE,{"disambiguationData":[TD([[makeQuery(id+"F0.imprint","IMPRINT",EDGE,{"derivedFrom":subQ0}),-1.0]])]});}
            var Q15;
            {var subQ0=sQuery(id+"F0.wireOp",EDGE,"E52.0.15.0");Q15=makeQuery(id+"F0.imprint","IMPRINT",FACE,{"disambiguationData":[TD([[makeQuery(id+"F0.imprint","IMPRINT",EDGE,{"derivedFrom":subQ0}),-1.0]])]});}
            var Q16;
            {var subQ0=sQuery(id+"F0.wireOp",EDGE,"E52.0.14.0");Q16=makeQuery(id+"F0.imprint","IMPRINT",FACE,{"disambiguationData":[TD([[makeQuery(id+"F0.imprint","IMPRINT",EDGE,{"derivedFrom":subQ0}),-1.0]])]});}
            var Q17;
            {var subQ0=sQuery(id+"F0.wireOp",EDGE,"E52.0.13.0");Q17=makeQuery(id+"F0.imprint","IMPRINT",FACE,{"disambiguationData":[TD([[makeQuery(id+"F0.imprint","IMPRINT",EDGE,{"derivedFrom":subQ0}),-1.0]])]});}
            var Q18;
            {var subQ0=sQuery(id+"F0.wireOp",EDGE,"E52.0.12.0");Q18=makeQuery(id+"F0.imprint","IMPRINT",FACE,{"disambiguationData":[TD([[makeQuery(id+"F0.imprint","IMPRINT",EDGE,{"derivedFrom":subQ0}),-1.0]])]});}
            var Q19;
            {var subQ0=sQuery(id+"F0.wireOp",EDGE,"E52.0.11.0");Q19=makeQuery(id+"F0.imprint","IMPRINT",FACE,{"disambiguationData":[TD([[makeQuery(id+"F0.imprint","IMPRINT",EDGE,{"derivedFrom":subQ0}),-1.0]])]});}
            var Q20;
            {var subQ0=sQuery(id+"F0.wireOp",EDGE,"E52.0.10.0");Q20=makeQuery(id+"F0.imprint","IMPRINT",FACE,{"disambiguationData":[TD([[makeQuery(id+"F0.imprint","IMPRINT",EDGE,{"derivedFrom":subQ0}),-1.0]])]});}
            var Q21;
            {var subQ0=sQuery(id+"F0.wireOp",EDGE,"E52.0.9.0");Q21=makeQuery(id+"F0.imprint","IMPRINT",FACE,{"disambiguationData":[TD([[makeQuery(id+"F0.imprint","IMPRINT",EDGE,{"derivedFrom":subQ0}),-1.0]])]});}
            var Q22;
            {var subQ0=sQuery(id+"F0.wireOp",EDGE,"E52.0.8.0");Q22=makeQuery(id+"F0.imprint","IMPRINT",FACE,{"disambiguationData":[TD([[makeQuery(id+"F0.imprint","IMPRINT",EDGE,{"derivedFrom":subQ0}),-1.0]])]});}
            var Q23;
            {var subQ0=sQuery(id+"F0.wireOp",EDGE,"E52.0.7.0");Q23=makeQuery(id+"F0.imprint","IMPRINT",FACE,{"disambiguationData":[TD([[makeQuery(id+"F0.imprint","IMPRINT",EDGE,{"derivedFrom":subQ0}),-1.0]])]});}
            var Q24;
            {var subQ0=sQuery(id+"F0.wireOp",EDGE,"E52.0.6.0");Q24=makeQuery(id+"F0.imprint","IMPRINT",FACE,{"disambiguationData":[TD([[makeQuery(id+"F0.imprint","IMPRINT",EDGE,{"derivedFrom":subQ0}),-1.0]])]});}
            var Q25;
            {var subQ0=sQuery(id+"F0.wireOp",EDGE,"E52.0.5.0");Q25=makeQuery(id+"F0.imprint","IMPRINT",FACE,{"disambiguationData":[TD([[makeQuery(id+"F0.imprint","IMPRINT",EDGE,{"derivedFrom":subQ0}),-1.0]])]});}
            var Q26;
            {var subQ0=sQuery(id+"F0.wireOp",EDGE,"E52.0.4.0");Q26=makeQuery(id+"F0.imprint","IMPRINT",FACE,{"disambiguationData":[TD([[makeQuery(id+"F0.imprint","IMPRINT",EDGE,{"derivedFrom":subQ0}),-1.0]])]});}
            var Q27;
            {var subQ0=sQuery(id+"F0.wireOp",EDGE,"E52.0.3.0");Q27=makeQuery(id+"F0.imprint","IMPRINT",FACE,{"disambiguationData":[TD([[makeQuery(id+"F0.imprint","IMPRINT",EDGE,{"derivedFrom":subQ0}),-1.0]])]});}
            var Q28;
            {var subQ0=sQuery(id+"F0.wireOp",EDGE,"E52.0.2.0");Q28=makeQuery(id+"F0.imprint","IMPRINT",FACE,{"disambiguationData":[TD([[makeQuery(id+"F0.imprint","IMPRINT",EDGE,{"derivedFrom":subQ0}),-1.0]])]});}
            var Q29;
            {var subQ0=sQuery(id+"F0.wireOp",EDGE,"E52.0.1.0");Q29=makeQuery(id+"F0.imprint","IMPRINT",FACE,{"disambiguationData":[TD([[makeQuery(id+"F0.imprint","IMPRINT",EDGE,{"derivedFrom":subQ0}),-1.0]])]});}
            var Q30;
            Q30=makeQuery(id+"F0.imprint","IMPRINT",FACE,{"disambiguationData":[TD([[makeQuery(id+"F0.imprint","IMPRINT",EDGE,{"derivedFrom":sQuery(id+"F0.wireOp",EDGE,"E51.bottom")}),-1.0]])]});
            var Q31;
            Q31=makeQuery(id+"F0.imprint","IMPRINT",FACE,{"disambiguationData":[TD([[makeQuery(id+"F0.imprint","IMPRINT",EDGE,{"derivedFrom":sQuery(id+"F0.wireOp",EDGE,"E14.bottom")}),1.0]])]});
            var Q32;
            Q32=makeQuery(id+"F0.imprint","IMPRINT",FACE,{"disambiguationData":[TD([[makeQuery(id+"F0.imprint","IMPRINT",EDGE,{"derivedFrom":sQuery(id+"F0.wireOp",EDGE,"E13.bottom")}),1.0]])]});
            var Q33;
            Q33=makeQuery(id+"F0.imprint","IMPRINT",FACE,{"disambiguationData":[TD([[makeQuery(id+"F0.imprint","IMPRINT",EDGE,{"derivedFrom":sQuery(id+"F0.wireOp",EDGE,"E16.MirrorCS")}),-1.0]])]});
            var Q34;
            Q34=makeQuery(id+"F0.imprint","IMPRINT",FACE,{"disambiguationData":[TD([[makeQuery(id+"F0.imprint","IMPRINT",EDGE,{"derivedFrom":sQuery(id+"F0.wireOp",EDGE,"E17.MirrorCS")}),-1.0]])]});
            var Q35;
            Q35=makeQuery(id+"F0.imprint","IMPRINT",FACE,{"disambiguationData":[TD([[makeQuery(id+"F0.imprint","IMPRINT",EDGE,{"derivedFrom":sQuery(id+"F0.wireOp",EDGE,"E68.MirrorCS")}),1.0]])]});
            var Q36;
            Q36=makeQuery(id+"F0.imprint","IMPRINT",FACE,{"disambiguationData":[TD([[makeQuery(id+"F0.imprint","IMPRINT",EDGE,{"derivedFrom":sQuery(id+"F0.wireOp",EDGE,"E59.MirrorCS")}),1.0]])]});
            var Q37;
            Q37=makeQuery(id+"F0.imprint","IMPRINT",FACE,{"disambiguationData":[TD([[makeQuery(id+"F0.imprint","IMPRINT",EDGE,{"derivedFrom":sQuery(id+"F0.wireOp",EDGE,"E62.MirrorCS")}),1.0]])]});
            var Q38;
            Q38=makeQuery(id+"F0.imprint","IMPRINT",FACE,{"disambiguationData":[TD([[makeQuery(id+"F0.imprint","IMPRINT",EDGE,{"derivedFrom":sQuery(id+"F0.wireOp",EDGE,"E67.MirrorCS")}),1.0]])]});
            var Q39;
            Q39=makeQuery(id+"F0.imprint","IMPRINT",FACE,{"disambiguationData":[TD([[makeQuery(id+"F0.imprint","IMPRINT",EDGE,{"derivedFrom":sQuery(id+"F0.wireOp",EDGE,"E57.MirrorCS")}),1.0]])]});
            var Q40;
            Q40=makeQuery(id+"F0.imprint","IMPRINT",FACE,{"disambiguationData":[TD([[makeQuery(id+"F0.imprint","IMPRINT",EDGE,{"derivedFrom":sQuery(id+"F0.wireOp",EDGE,"E65.MirrorCS")}),1.0]])]});
            var Q41;
            Q41=makeQuery(id+"F0.imprint","IMPRINT",FACE,{"disambiguationData":[TD([[makeQuery(id+"F0.imprint","IMPRINT",EDGE,{"derivedFrom":sQuery(id+"F0.wireOp",EDGE,"E53.MirrorCS")}),1.0]])]});
            var Q42;
            Q42=makeQuery(id+"F0.imprint","IMPRINT",FACE,{"disambiguationData":[TD([[makeQuery(id+"F0.imprint","IMPRINT",EDGE,{"derivedFrom":sQuery(id+"F0.wireOp",EDGE,"E60.MirrorCS")}),1.0]])]});
            var Q43;
            Q43=makeQuery(id+"F0.imprint","IMPRINT",FACE,{"disambiguationData":[TD([[makeQuery(id+"F0.imprint","IMPRINT",EDGE,{"derivedFrom":sQuery(id+"F0.wireOp",EDGE,"E63.MirrorCS")}),1.0]])]});
            var Q44;
            Q44=makeQuery(id+"F0.imprint","IMPRINT",FACE,{"disambiguationData":[TD([[makeQuery(id+"F0.imprint","IMPRINT",EDGE,{"derivedFrom":sQuery(id+"F0.wireOp",EDGE,"E58.MirrorCS")}),1.0]])]});
            var Q45;
            Q45=makeQuery(id+"F0.imprint","IMPRINT",FACE,{"disambiguationData":[TD([[makeQuery(id+"F0.imprint","IMPRINT",EDGE,{"derivedFrom":sQuery(id+"F0.wireOp",EDGE,"E54.MirrorCS")}),1.0]])]});
            var Q46;
            Q46=makeQuery(id+"F0.imprint","IMPRINT",FACE,{"disambiguationData":[TD([[makeQuery(id+"F0.imprint","IMPRINT",EDGE,{"derivedFrom":sQuery(id+"F0.wireOp",EDGE,"E66.MirrorCS")}),1.0]])]});
            var Q47;
            Q47=makeQuery(id+"F0.imprint","IMPRINT",FACE,{"disambiguationData":[TD([[makeQuery(id+"F0.imprint","IMPRINT",EDGE,{"derivedFrom":sQuery(id+"F0.wireOp",EDGE,"E55.MirrorCS")}),1.0]])]});
            var Q48;
            Q48=makeQuery(id+"F0.imprint","IMPRINT",FACE,{"disambiguationData":[TD([[makeQuery(id+"F0.imprint","IMPRINT",EDGE,{"derivedFrom":sQuery(id+"F0.wireOp",EDGE,"E64.MirrorCS")}),1.0]])]});
            extrude(context, id + "F2", {"entities" : qUnion([Q0, Q1, Q2, Q3, Q4, Q5, Q6, Q7, Q8, Q9, Q10, Q11, Q12, Q13, Q14, Q15, Q16, Q17, Q18, Q19, Q20, Q21, Q22, Q23, Q24, Q25, Q26, Q27, Q28, Q29, Q30, Q31, Q32, Q33, Q34, Q35, Q36, Q37, Q38, Q39, Q40, Q41, Q42, Q43, Q44, Q45, Q46, Q47, Q48]), "operationType" : NewBodyOperationType.ADD, "depth" : 2 * mm});
        }
        {
            var Q0;
            {var subQ0=sQuery(id+"F0.wireOp",EDGE,"E6");Q0=makeQuery(id+"F0.imprint","IMPRINT",FACE,{"disambiguationData":[TD([[makeQuery(id+"F0.imprint","IMPRINT",EDGE,{"derivedFrom":subQ0}),-1.0]])]});}
            var Q1;
            {var subQ0=sQuery(id+"F0.wireOp",EDGE,"E1.right");Q1=makeQuery(id+"F0.imprint","IMPRINT",FACE,{"disambiguationData":[TD([[makeQuery(id+"F0.imprint","IMPRINT",EDGE,{"derivedFrom":subQ0}),1.0]])]});}
            var Q2;
            {var subQ0=sQuery(id+"F0.wireOp",EDGE,"E5");Q2=makeQuery(id+"F0.imprint","IMPRINT",FACE,{"disambiguationData":[TD([[makeQuery(id+"F0.imprint","IMPRINT",EDGE,{"derivedFrom":subQ0}),1.0]])]});}
            var Q3;
            {var subQ0=sQuery(id+"F0.wireOp",EDGE,"E7");Q3=makeQuery(id+"F0.imprint","IMPRINT",FACE,{"disambiguationData":[TD([[makeQuery(id+"F0.imprint","IMPRINT",EDGE,{"derivedFrom":subQ0}),1.0]])]});}
            var Q4;
            {var subQ0=sQuery(id+"F0.wireOp",EDGE,"E1.left");Q4=makeQuery(id+"F0.imprint","IMPRINT",FACE,{"disambiguationData":[TD([[makeQuery(id+"F0.imprint","IMPRINT",EDGE,{"derivedFrom":subQ0}),-1.0]])]});}
            extrude(context, id + "F3", {"entities" : qUnion([Q0, Q1, Q2, Q3, Q4]), "depth" : 1 * mm});
        }
        {
            var Q0;
            {var subQ0=sQuery(id+"F0.wireOp",EDGE,"E1.left");Q0=makeQuery(id+"F0.imprint","IMPRINT",FACE,{"disambiguationData":[TD([[makeQuery(id+"F0.imprint","IMPRINT",EDGE,{"derivedFrom":subQ0}),-1.0]])]});}
            var Q1;
            {var subQ0=sQuery(id+"F0.wireOp",EDGE,"E5");Q1=makeQuery(id+"F0.imprint","IMPRINT",FACE,{"disambiguationData":[TD([[makeQuery(id+"F0.imprint","IMPRINT",EDGE,{"derivedFrom":subQ0}),1.0]])]});}
            var Q2;
            {var subQ0=sQuery(id+"F0.wireOp",EDGE,"E6");Q2=makeQuery(id+"F0.imprint","IMPRINT",FACE,{"disambiguationData":[TD([[makeQuery(id+"F0.imprint","IMPRINT",EDGE,{"derivedFrom":subQ0}),-1.0]])]});}
            var Q3;
            {var subQ0=sQuery(id+"F0.wireOp",EDGE,"E1.right");Q3=makeQuery(id+"F0.imprint","IMPRINT",FACE,{"disambiguationData":[TD([[makeQuery(id+"F0.imprint","IMPRINT",EDGE,{"derivedFrom":subQ0}),1.0]])]});}
            extrude(context, id + "F4", {"entities" : qUnion([Q0, Q1, Q2, Q3]), "operationType" : NewBodyOperationType.ADD, "depth" : 5 * mm});
        }
        {
            var Q0;
            {var subQ0=sQuery(id+"F0.wireOp",EDGE,"E1.left");Q0=makeQuery(id+"F0.imprint","IMPRINT",FACE,{"disambiguationData":[TD([[makeQuery(id+"F0.imprint","IMPRINT",EDGE,{"derivedFrom":subQ0}),-1.0]])]});}
            var Q1;
            {var subQ0=sQuery(id+"F0.wireOp",EDGE,"E1.right");Q1=makeQuery(id+"F0.imprint","IMPRINT",FACE,{"disambiguationData":[TD([[makeQuery(id+"F0.imprint","IMPRINT",EDGE,{"derivedFrom":subQ0}),1.0]])]});}
            extrude(context, id + "F5", {"entities" : qUnion([Q0, Q1]), "operationType" : NewBodyOperationType.ADD, "depth" : 7 * mm});
        }
        {
            var Q0;
            {var subQ0=sQuery(id+"F0.wireOp",EDGE,"E116");var subQ1=sQuery(id+"F0.wireOp",EDGE,"E3.top");var subQ2=makeQuery(id+"F0.imprint","INTERSECT",VERTEX,{"disambiguationData":[OD(0.0)],"derivedFrom":[subQ1,subQ0]});Q0=makeQuery(id+"F0.imprint","IMPRINT",FACE,{"disambiguationData":[TD([[makeQuery(id+"F0.imprint","IMPRINT",EDGE,{"disambiguationData":[TD([[subQ2,-1.0]])],"derivedFrom":subQ1}),1.0]])]});}
            var Q1;
            {var subQ0=sQuery(id+"F0.wireOp",EDGE,"E3.left");Q1=makeQuery(id+"F0.imprint","IMPRINT",FACE,{"disambiguationData":[TD([[makeQuery(id+"F0.imprint","IMPRINT",EDGE,{"derivedFrom":subQ0}),-1.0]])]});}
            var Q2;
            {var subQ0=sQuery(id+"F0.wireOp",EDGE,"E3.right");Q2=makeQuery(id+"F0.imprint","IMPRINT",FACE,{"disambiguationData":[TD([[makeQuery(id+"F0.imprint","IMPRINT",EDGE,{"derivedFrom":subQ0}),1.0]])]});}
            var Q3;
            {var subQ0=sQuery(id+"F0.wireOp",EDGE,"E116");var subQ1=sQuery(id+"F0.wireOp",EDGE,"E3.top");var subQ2=makeQuery(id+"F0.imprint","INTERSECT",VERTEX,{"disambiguationData":[OD(0.0)],"derivedFrom":[subQ1,subQ0]});Q3=makeQuery(id+"F0.imprint","IMPRINT",FACE,{"disambiguationData":[TD([[makeQuery(id+"F0.imprint","IMPRINT",EDGE,{"disambiguationData":[TD([[subQ2,-1.0]])],"derivedFrom":subQ1}),-1.0]])]});}
            var Q4;
            {var subQ0=sQuery(id+"F0.wireOp",EDGE,"E115");var subQ1=sQuery(id+"F0.wireOp",EDGE,"E3.top");var subQ2=makeQuery(id+"F0.imprint","INTERSECT",VERTEX,{"disambiguationData":[OD(0.0)],"derivedFrom":[subQ1,subQ0]});Q4=makeQuery(id+"F0.imprint","IMPRINT",FACE,{"disambiguationData":[TD([[makeQuery(id+"F0.imprint","IMPRINT",EDGE,{"disambiguationData":[TD([[subQ2,-1.0]])],"derivedFrom":subQ1}),-1.0]])]});}
            extrude(context, id + "F6", {"entities" : qUnion([Q0, Q1, Q2, Q3, Q4]), "depth" : 1.5 * mm});
        }
        {
            var Q0;
            {var subQ0=sQuery(id+"F0.wireOp",EDGE,"E3.right");Q0=makeQuery(id+"F0.imprint","IMPRINT",FACE,{"disambiguationData":[TD([[makeQuery(id+"F0.imprint","IMPRINT",EDGE,{"derivedFrom":subQ0}),1.0]])]});}
            extrude(context, id + "F7", {"entities" : qUnion([Q0]), "operationType" : NewBodyOperationType.ADD, "depth" : 2.5 * mm});
        }
        {
            var Q0;
            Q0=makeQuery(id+"F0.imprint","IMPRINT",FACE,{"disambiguationData":[TD([[makeQuery(id+"F0.imprint","IMPRINT",EDGE,{"derivedFrom":sQuery(id+"F0.wireOp",EDGE,"E2.bottom")}),1.0]])]});
            extrude(context, id + "F8", {"entities" : qUnion([Q0]), "depth" : 1 * mm});
        }
        {
            var Q0;
            Q0=makeQuery(id+"F0.imprint","IMPRINT",FACE,{"disambiguationData":[TD([[makeQuery(id+"F0.imprint","IMPRINT",EDGE,{"derivedFrom":sQuery(id+"F0.wireOp",EDGE,"E4.bottom")}),1.0]])]});
            extrude(context, id + "F9", {"entities" : qUnion([Q0]), "depth" : 1 * mm});
        }
    });
